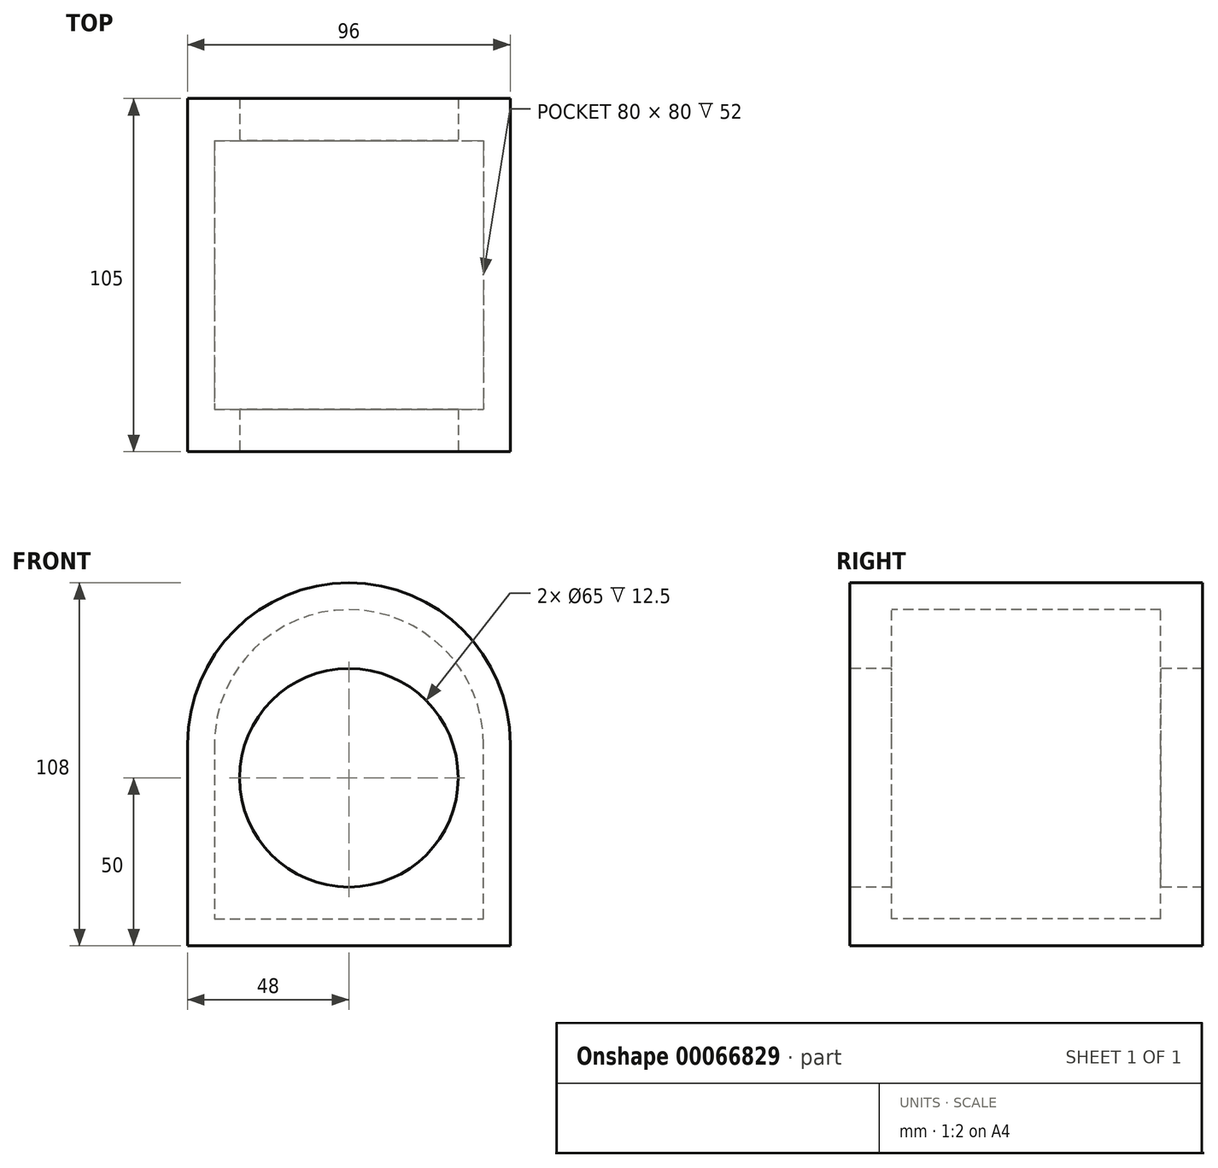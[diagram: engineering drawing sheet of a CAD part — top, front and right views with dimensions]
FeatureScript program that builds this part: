
annotation { "Feature Type Name" : "Feature", "Feature Type Description" : "" }
export const myFeature = defineFeature(function(context is Context, id is Id, definition is map)
    precondition{}
    {
        {
            var Q0;
            Q0=qCreatedBy(makeId("Front.planeOp"),FACE);
            cPlane(context, id + "F0", {"entities" : qUnion([Q0]), "cplaneType" : CPlaneType.OFFSET, "offset" : 40 * mm, "width" : 150 * mm, "height" : 150 * mm});
        }
        {
            var Q0;
            Q0=qCreatedBy(id+"F0.planeOp",FACE);
            var sketch = newSketch(context, id + "F1", { "sketchPlane" : qUnion([Q0])});
            skArc(sketch, "E0", {"start": v(48, 60) * mm, "mid": v(0, 108) * mm, "end": v(-48, 60) * mm});
            skLineSegment(sketch, "E1", {"start": v(-48, 60) * mm, "end": v(-48, 0) * mm});
            skLineSegment(sketch, "E2", {"start": v(-48, 0) * mm, "end": v(48, 0) * mm});
            skLineSegment(sketch, "E3", {"start": v(48, 0) * mm, "end": v(48, 60) * mm});
            skSolve(sketch);
        }
        {
            var Q0;
            Q0=makeQuery(id+"F1.imprint","IMPRINT",FACE,{"disambiguationData":[TD([[makeQuery(id+"F1.imprint","IMPRINT",EDGE,{"derivedFrom":sQuery(id+"F1.wireOp",EDGE,"E0")}),1.0]])]});
            extrude(context, id + "F2", {"entities" : qUnion([Q0]), "depth" : 12.5 * mm});
        }
        {
            var Q0;
            Q0=makeQuery(id+"F2.opExtrude","CAP_FACE",FACE,{"disambiguationData":[OSD([sQuery(id+"F1.wireOp",EDGE,"E0"),sQuery(id+"F1.wireOp",EDGE,"E1"),sQuery(id+"F1.wireOp",EDGE,"E2"),sQuery(id+"F1.wireOp",EDGE,"E3")])],"isStart":true});
            var sketch = newSketch(context, id + "F3", { "sketchPlane" : qUnion([Q0])});
            skArc(sketch, "E4.0", {"start": v(-40, 60) * mm, "mid": v(0, 100) * mm, "end": v(40, 60) * mm});
            skLineSegment(sketch, "E4.1", {"start": v(-40, 8) * mm, "end": v(-40, 60) * mm});
            skLineSegment(sketch, "E4.2", {"start": v(40, 8) * mm, "end": v(-40, 8) * mm});
            skLineSegment(sketch, "E4.3", {"start": v(40, 60) * mm, "end": v(40, 8) * mm});
            skSolve(sketch);
        }
        {
            var Q0;
            Q0=makeQuery(id+"F3.imprint","IMPRINT",FACE,{"disambiguationData":[TD([[makeQuery(id+"F3.imprint","IMPRINT",EDGE,{"derivedFrom":sQuery(id+"F3.wireOp",EDGE,"E4.0")}),-1.0]])]});
            var Q1;
            Q1=qCreatedBy(makeId("Front.planeOp"),FACE);
            extrude(context, id + "F4", {"entities" : qUnion([Q0]), "operationType" : NewBodyOperationType.ADD, "endBound" : BoundingType.UP_TO_SURFACE, "endBoundEntityFace" : qUnion([Q1]), "depth" : 25 * mm});
        }
        {
            var Q0;
            Q0=makeQuery(id+"F2.opExtrude","SWEPT_BODY",BODY,{"disambiguationData":[OSD([sQuery(id+"F1.wireOp",EDGE,"E0"),sQuery(id+"F1.wireOp",EDGE,"E1"),sQuery(id+"F1.wireOp",EDGE,"E2"),sQuery(id+"F1.wireOp",EDGE,"E3")])]});
            var Q1;
            Q1=qCreatedBy(makeId("Front.planeOp"),FACE);
            mirror(context, id + "F5", {"operationType" : NewBodyOperationType.ADD, "entities" : qUnion([Q0]), "mirrorPlane" : qUnion([Q1])});
        }
        {
            var Q0;
            Q0=makeQuery(id+"F2.opExtrude","CAP_FACE",FACE,{"disambiguationData":[OSD([sQuery(id+"F1.wireOp",EDGE,"E0"),sQuery(id+"F1.wireOp",EDGE,"E1"),sQuery(id+"F1.wireOp",EDGE,"E2"),sQuery(id+"F1.wireOp",EDGE,"E3")])],"isStart":false});
            var sketch = newSketch(context, id + "F6", { "sketchPlane" : qUnion([Q0])});
            skCircle(sketch, "E5", {"center": v(0, 50) * mm, "radius": 32.5 * mm});
            skSolve(sketch);
        }
        {
            var Q0;
            Q0=makeQuery(id+"F6.imprint","IMPRINT",FACE,{"disambiguationData":[TD([[makeQuery(id+"F6.imprint","IMPRINT",EDGE,{"derivedFrom":sQuery(id+"F6.wireOp",EDGE,"E5")}),1.0]])]});
            extrude(context, id + "F7", {"entities" : qUnion([Q0]), "operationType" : NewBodyOperationType.REMOVE, "endBound" : BoundingType.THROUGH_ALL, "oppositeDirection" : true, "depth" : 25 * mm});
        }
    });
